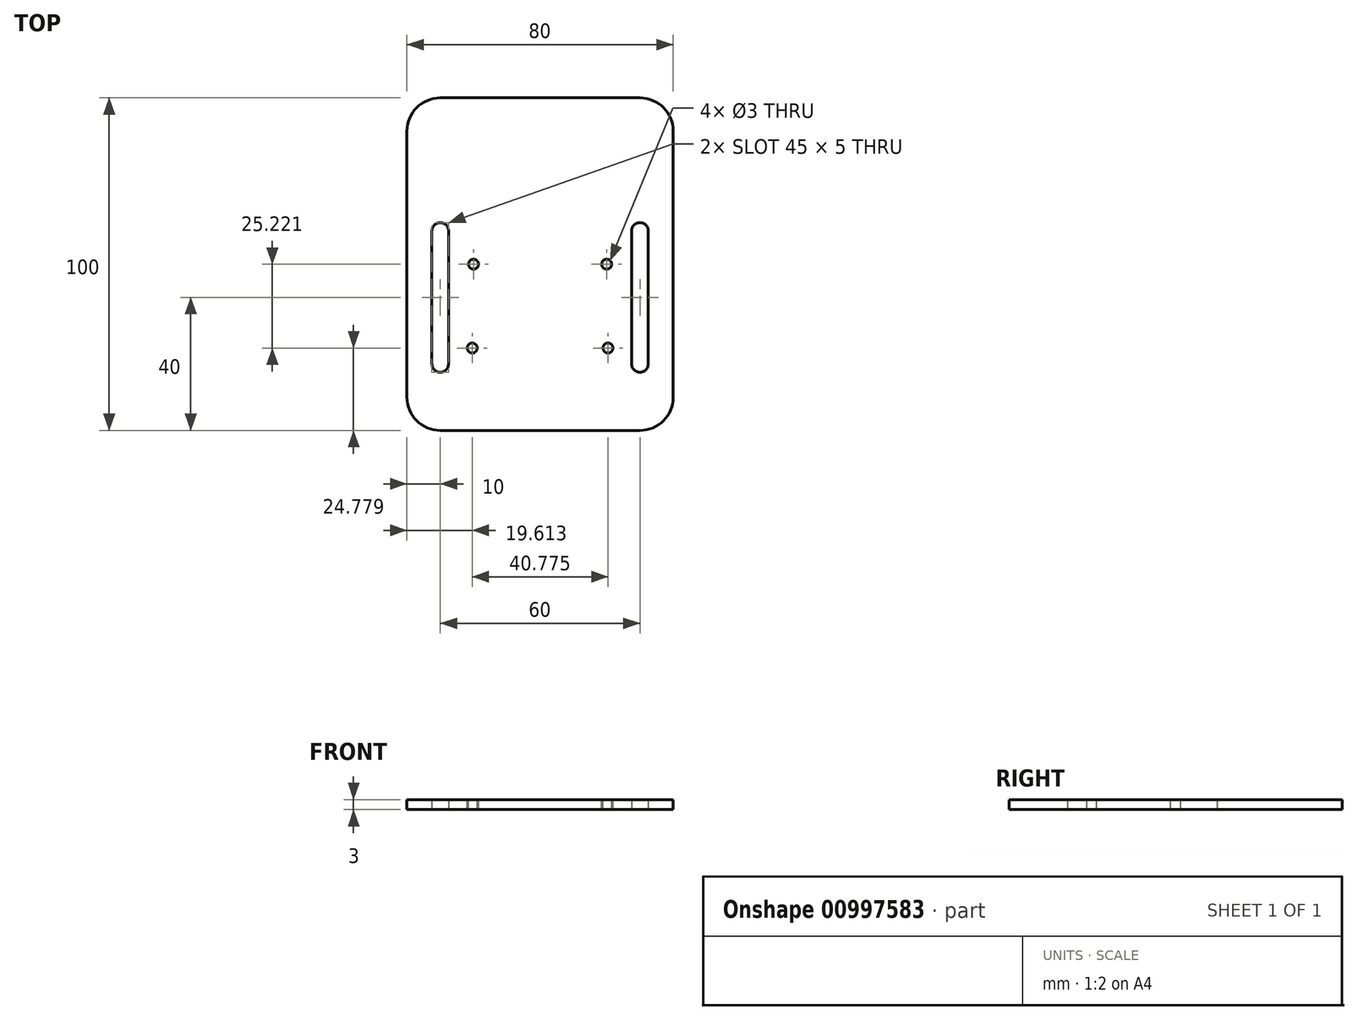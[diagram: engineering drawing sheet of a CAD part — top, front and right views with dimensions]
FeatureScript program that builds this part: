
annotation { "Feature Type Name" : "Feature", "Feature Type Description" : "" }
export const myFeature = defineFeature(function(context is Context, id is Id, definition is map)
    precondition{}
    {
        {
            var Q0;
            Q0=qCreatedBy(makeId("Top.planeOp"),FACE);
            var sketch = newSketch(context, id + "F0", { "sketchPlane" : qUnion([Q0])});
            skLineSegment(sketch, "E0.bottom", {"start": v(0, 0) * mm, "end": v(40, 0) * mm});
            skLineSegment(sketch, "E0.top", {"start": v(0, 100) * mm, "end": v(40, 100) * mm});
            skLineSegment(sketch, "E0.left", {"start": v(0, 0) * mm, "end": v(0, 100) * mm});
            skLineSegment(sketch, "E0.right", {"start": v(40, 0) * mm, "end": v(40, 100) * mm});
            skSolve(sketch);
        }
        {
            var Q0;
            Q0=makeQuery(id+"F0.imprint","IMPRINT",FACE,{"disambiguationData":[TD([[makeQuery(id+"F0.imprint","IMPRINT",EDGE,{"derivedFrom":sQuery(id+"F0.wireOp",EDGE,"E0.bottom")}),1.0]])]});
            extrude(context, id + "F1", {"entities" : qUnion([Q0]), "depth" : 3 * mm, "offsetDistance" : 25 * mm});
        }
        {
            var Q0;
            Q0=makeQuery(id+"F1.opExtrude","CAP_FACE",FACE,{"disambiguationData":[OSD([sQuery(id+"F0.wireOp",EDGE,"E0.bottom"),sQuery(id+"F0.wireOp",EDGE,"E0.top"),sQuery(id+"F0.wireOp",EDGE,"E0.left"),sQuery(id+"F0.wireOp",EDGE,"E0.right")])],"isStart":false});
            var sketch = newSketch(context, id + "F2", { "sketchPlane" : qUnion([Q0])});
            skLineSegment(sketch, "E1", {"start": v(20, 25) * mm, "end": v(20, 50) * mm});
            skSolve(sketch);
        }
        {
            var Q0;
            Q0=makeQuery(id+"F2.imprint","IMPRINT",FACE,{"disambiguationData":[TD([[makeQuery(id+"F2.imprint","IMPRINT",EDGE,{"derivedFrom":makeQuery(id+"F1.opExtrude","CAP_EDGE",EDGE,{"disambiguationData":[OSD([sQuery(id+"F0.wireOp",EDGE,"E0.bottom")])],"isStart":false})}),1.0]])]});
            var sketch = newSketch(context, id + "F3", { "sketchPlane" : qUnion([Q0])});
            skPoint(sketch, "E2", {"position": v(18.9, 51.04) * mm});
            skPoint(sketch, "E3", {"position": v(20.39, 24.78) * mm});
            skSolve(sketch);
        }
        {
            var Q0;
            Q0=sQuery(id+"F2.wireOp",VERTEX,"E1.end");
            var Q1;
            Q1=sQuery(id+"F3.wireOp",VERTEX,"E3");
            var Q2;
            Q2=makeQuery(id+"F1.opExtrude","SWEPT_BODY",BODY,{"disambiguationData":[OSD([sQuery(id+"F0.wireOp",EDGE,"E0.bottom"),sQuery(id+"F0.wireOp",EDGE,"E0.top"),sQuery(id+"F0.wireOp",EDGE,"E0.left"),sQuery(id+"F0.wireOp",EDGE,"E0.right")])]});
            hole(context, id + "F4", {"style" : HoleStyle.SIMPLE, "endStyle" : HoleEndStyle.THROUGH, "holeDiameter" : 3 * mm, "majorDiameter" : 5 * mm, "isTappedThrough" : true, "tappedDepth" : 12 * mm, "tapClearance" : 3, "locations" : qUnion([Q0, Q1]), "scope" : qUnion([Q2])});
        }
        {
            var Q0;
            Q0=qCreatedBy(makeId("Top.planeOp"),FACE);
            var sketch = newSketch(context, id + "F5", { "sketchPlane" : qUnion([Q0])});
            skLineSegment(sketch, "E4", {"start": v(30, 20) * mm, "end": v(30, 60) * mm});
            skArc(sketch, "E5.0.startCap", {"start": v(32.5, 20) * mm, "mid": v(30, 17.5) * mm, "end": v(27.5, 20) * mm});
            skArc(sketch, "E5.0.endCap", {"start": v(27.5, 60) * mm, "mid": v(30, 62.5) * mm, "end": v(32.5, 60) * mm});
            skLineSegment(sketch, "E5.0.left", {"start": v(27.5, 20) * mm, "end": v(27.5, 60) * mm});
            skLineSegment(sketch, "E5.0.right", {"start": v(32.5, 20) * mm, "end": v(32.5, 60) * mm});
            skSolve(sketch);
        }
        {
            var Q0;
            Q0 = qSketchRegion(id + "F5", true);
            extrude(context, id + "F6", {"entities" : qUnion([Q0]), "operationType" : NewBodyOperationType.REMOVE, "oppositeDirection" : true, "depth" : 35.19 * mm, "offsetDistance" : 25 * mm});
        }
        {
            var Q0;
            Q0 = qSketchRegion(id + "F5", true);
            extrude(context, id + "F7", {"entities" : qUnion([Q0]), "operationType" : NewBodyOperationType.REMOVE, "depth" : 100.8 * mm, "offsetDistance" : 25 * mm});
        }
        {
            var Q0;
            Q0=makeQuery(id+"F1.opExtrude","SWEPT_EDGE",EDGE,{"disambiguationData":[OSD([sQuery(id+"F0.wireOp",EDGE,"E0.top"),sQuery(id+"F0.wireOp",EDGE,"E0.right")])]});
            var Q1;
            Q1=makeQuery(id+"F1.opExtrude","SWEPT_EDGE",EDGE,{"disambiguationData":[OSD([sQuery(id+"F0.wireOp",EDGE,"E0.bottom"),sQuery(id+"F0.wireOp",EDGE,"E0.right")])]});
            fillet(context, id + "F8", {"entities" : qUnion([Q0, Q1]), "radius" : 10 * mm, "tangentPropagation" : true, "allowEdgeOverflow" : false});
        }
        {
            var Q0;
            Q0=makeQuery(id+"F1.opExtrude","SWEPT_BODY",BODY,{"disambiguationData":[OSD([sQuery(id+"F0.wireOp",EDGE,"E0.bottom"),sQuery(id+"F0.wireOp",EDGE,"E0.top"),sQuery(id+"F0.wireOp",EDGE,"E0.left"),sQuery(id+"F0.wireOp",EDGE,"E0.right")])]});
            var Q1;
            Q1=qCreatedBy(makeId("Right.planeOp"),FACE);
            mirror(context, id + "F9", {"operationType" : NewBodyOperationType.ADD, "entities" : qUnion([Q0]), "mirrorPlane" : qUnion([Q1])});
        }
    });
